# Revit family: Gira_017730
name_source: partatom
category: Electrical Fixtures
revit_build: Autodesk Revit 2017 (Build: 20160225_1515(x64)
units: mm (PartAtom-declared; Revit-internal decimal feet)

## family parameters
Cut with Voids When Loaded = No
Host = Face
Maintain Annotation Orientation = Yes
Part Type = Normal
Room Calculation Point = No
Round Connector Dimension = Use Diameter
Shared = No

## types (1)
- Gira_017730
    Anzahl der Steckdosen = 1
    Ausführung der Steckdose = Schuko
    Ausführung des Schalters = Wechselschalter
    Available = Yes
    Bedienungsart = Wippe/Taste
    Befestigungsart = Befestigung mit Schraube
    Category = Schalter-/Steckdosenkombination
    Data sheet (1) = https://katalog.gira.de
    Default Elevation = 1219 mm
    Farbe = weiß
    GTIN = 4010337177302
    Geeignet für Schutzart (IP) = IP44
    HAN = 017730
    Halogenfrei = No
    HeinzeBIM = https://bimportal.heinze.de
    Keynote = IP44_Komplettgerät_Steckdose_2fach
    Manufacturer URL = https://www.gira.de
    Mit Beleuchtung = No
    Montageart = auf Putz
    Montagerichtung = horizontal
    Name = Kombi AusWe/SCHUKO waager. KD WG AP Grau
    Nennspannung = 250 Volt
    Nennstrom Steckdose = 16 Ampere
    Oberfläche = sonstige
    Region = DE
    URL = http://katalog.gira.de
    Werkstoff = sonstige
    Werkstoffgüte = sonstige

## geometry (parser evidence)
native form markers: Sweep x4
no freeform markers — native parametric forms only
